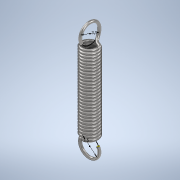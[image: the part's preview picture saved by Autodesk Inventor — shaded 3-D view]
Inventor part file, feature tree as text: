
AUTODESK INVENTOR PART (.ipt)
format: ipt  version: 2020.1 (Build 241239000, 239)  size: 660,992 bytes
history: native  units: mm
features: sketch x10, other x4, plane x2, sweep x2, helix x1
ambient origin geometry x8: Origin, YZ Plane, XZ Plane, XY Plane, X Axis, Y Axis, Z Axis, Center Point
bodies: Solid1 (feature_tree)
feature tree (19):
  helix  "Coil1"  [1 undecoded]
  plane  "Work Plane5"
  sketch  "Sketch15"  dims[d3=10.0mm d4=14.3mm d5=272.5mm d6=0.0mm d7=90.0deg d8=90.0deg d9=6.981317mm d10=0.0mm d35=0.0mm]
  sweep  "Sweep5"
  plane  "Work Plane6"
  sketch  "Sketch17"  dims[d37=0.0mm d38=0.0mm]
  sketch  "Sketch18"  dims[d39=0.0mm]
  sweep  "Sweep6"
  sketch  "Sketch20"  dims[d41=0.0mm d42=0.0mm]
  sketch  "Sketch21"  dims[d45=3.5mm d46=3.5mm d47=10.995574mm d48=10.995574mm]
  sketch  "Sketch1"  dims[d1=0.5mm d2=1.565mm]
  other  "Work Axis2"
  sketch  "3D Sketch8"
  other  "3D Intersection3"
  sketch  "Sketch16"  dims[d36=1.75mm]
  other  "Work Axis3"
  sketch  "3D Sketch9"
  other  "3D Intersection4"
  sketch  "Sketch19"  dims[d40=1.75mm]
note: 1 required parameter value undecoded (feature->parameter linkage not recoverable at this tier; creation-order binding heuristic only, values carry confidence <= 0.55)
